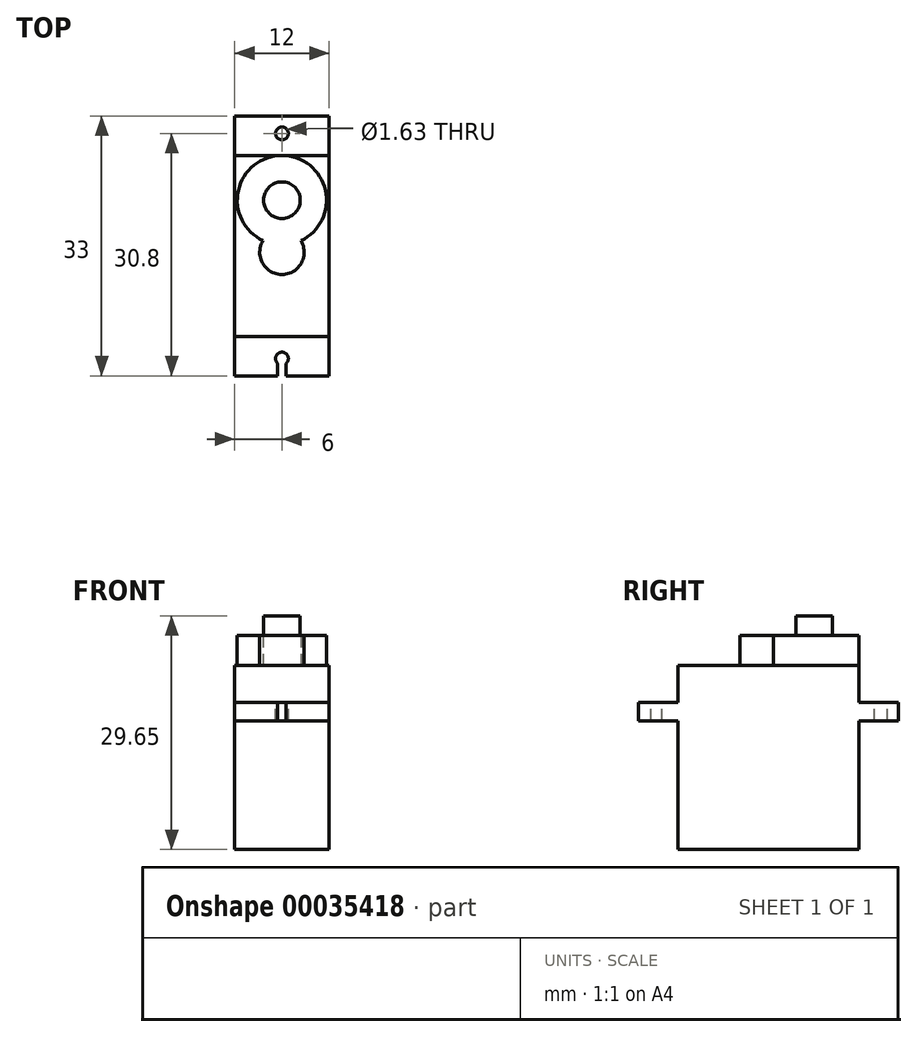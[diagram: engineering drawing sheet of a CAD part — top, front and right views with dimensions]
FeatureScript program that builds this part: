
annotation { "Feature Type Name" : "Feature", "Feature Type Description" : "" }
export const myFeature = defineFeature(function(context is Context, id is Id, definition is map)
    precondition{}
    {
        {
            var Q0;
            Q0=qCreatedBy(makeId("Top.planeOp"),FACE);
            var sketch = newSketch(context, id + "F0", { "sketchPlane" : qUnion([Q0])});
            skLineSegment(sketch, "E0.rect.bottom", {"start": v(-6, -11.5) * mm, "end": v(6, -11.5) * mm});
            skLineSegment(sketch, "E0.rect.top", {"start": v(-6, 11.5) * mm, "end": v(6, 11.5) * mm});
            skLineSegment(sketch, "E0.rect.left", {"start": v(-6, -11.5) * mm, "end": v(-6, 11.5) * mm});
            skLineSegment(sketch, "E0.rect.right", {"start": v(6, -11.5) * mm, "end": v(6, 11.5) * mm});
            skPoint(sketch, "E0.rect.middle", {"position": v(0, 0) * mm});
            skSolve(sketch);
        }
        {
            var Q0;
            Q0 = qSketchRegion(id + "F0", true);
            extrude(context, id + "F1", {"entities" : qUnion([Q0]), "depth" : 23.35 * mm});
        }
        {
            var Q0;
            Q0=makeQuery(id+"F1.opExtrude","SWEPT_FACE",FACE,{"disambiguationData":[OSD([sQuery(id+"F0.wireOp",EDGE,"E0.rect.bottom")])]});
            var sketch = newSketch(context, id + "F2", { "sketchPlane" : qUnion([Q0])});
            skLineSegment(sketch, "E1", {"start": v(-6, 23.35) * mm, "end": v(-6, 16.35) * mm});
            skLineSegment(sketch, "E2", {"start": v(-6, 16.35) * mm, "end": v(-6, 23.35) * mm});
            skLineSegment(sketch, "E3.bottom", {"start": v(-6, 16.35) * mm, "end": v(6, 16.35) * mm});
            skLineSegment(sketch, "E3.top", {"start": v(-6, 18.65) * mm, "end": v(6, 18.65) * mm});
            skLineSegment(sketch, "E3.left", {"start": v(-6, 16.35) * mm, "end": v(-6, 18.65) * mm});
            skLineSegment(sketch, "E3.right", {"start": v(6, 16.35) * mm, "end": v(6, 18.65) * mm});
            skSolve(sketch);
        }
        {
            var Q0;
            Q0 = qSketchRegion(id + "F2", true);
            extrude(context, id + "F3", {"entities" : qUnion([Q0]), "operationType" : NewBodyOperationType.ADD, "depth" : 5 * mm, "hasSecondDirection" : true, "secondDirectionOppositeDirection" : true, "secondDirectionDepth" : 28 * mm});
        }
        {
            var Q0;
            Q0=makeQuery(id+"F1.opExtrude","CAP_FACE",FACE,{"disambiguationData":[OSD([sQuery(id+"F0.wireOp",EDGE,"E0.rect.bottom"),sQuery(id+"F0.wireOp",EDGE,"E0.rect.top"),sQuery(id+"F0.wireOp",EDGE,"E0.rect.left"),sQuery(id+"F0.wireOp",EDGE,"E0.rect.right")])],"isStart":false});
            var sketch = newSketch(context, id + "F4", { "sketchPlane" : qUnion([Q0])});
            skLineSegment(sketch, "E4", {"start": v(0, 11.5) * mm, "end": v(0, 5.82) * mm});
            skPoint(sketch, "E4.endSnap0", {"position": v(0, 11.5) * mm});
            skLineSegment(sketch, "E5", {"start": v(0, 5.82) * mm, "end": v(0, 11.5) * mm});
            skCircle(sketch, "E6", {"center": v(0, 5.82) * mm, "radius": 5.68 * mm});
            skLineSegment(sketch, "E7", {"start": v(0, 11.5) * mm, "end": v(0, -0.8) * mm});
            skLineSegment(sketch, "E8", {"start": v(0, -0.8) * mm, "end": v(0, 11.5) * mm});
            skCircle(sketch, "E9", {"center": v(0, -0.8) * mm, "radius": 2.83 * mm});
            skSolve(sketch);
        }
        {
            var Q0;
            Q0 = qSketchRegion(id + "F4", true);
            extrude(context, id + "F5", {"entities" : qUnion([Q0]), "operationType" : NewBodyOperationType.ADD, "depth" : 3.8 * mm});
        }
        {
            var Q0;
            Q0=makeQuery(id+"F5.opExtrude","CAP_FACE",FACE,{"disambiguationData":[OSD([sQuery(id+"F4.wireOp",EDGE,"E6"),sQuery(id+"F4.wireOp",EDGE,"E9")])],"isStart":false});
            var sketch = newSketch(context, id + "F6", { "sketchPlane" : qUnion([Q0])});
            skCircle(sketch, "E10", {"center": v(0, 5.82) * mm, "radius": 2.33 * mm});
            skSolve(sketch);
        }
        {
            var Q0;
            Q0 = qSketchRegion(id + "F6", true);
            extrude(context, id + "F7", {"entities" : qUnion([Q0]), "operationType" : NewBodyOperationType.ADD, "depth" : 2.5 * mm});
        }
        {
            var Q0;
            {var subQ2=sQuery(id+"F2.wireOp",EDGE,"E3.top");Q0=makeQuery(id+"F3.boolean.opBoolean","SPLIT",FACE,{"disambiguationData":[TD([makeQuery(id+"F1.opExtrude","SWEPT_FACE",FACE,{"disambiguationData":[OSD([sQuery(id+"F0.wireOp",EDGE,"E0.rect.top")])]})])],"derivedFrom":makeQuery(id+"F3.opExtrude","SWEPT_FACE",FACE,{"disambiguationData":[OSD([subQ2])]})});}
            var sketch = newSketch(context, id + "F8", { "sketchPlane" : qUnion([Q0])});
            skLineSegment(sketch, "E11.bottom", {"start": v(-6, 16.5) * mm, "end": v(6, 16.5) * mm});
            skLineSegment(sketch, "E11.top", {"start": v(-6, 16.5) * mm, "end": v(6, 16.5) * mm});
            skLineSegment(sketch, "E11.left", {"start": v(-6, 16.5) * mm, "end": v(-6, 16.5) * mm});
            skLineSegment(sketch, "E11.right", {"start": v(6, 16.5) * mm, "end": v(6, 16.5) * mm});
            skLineSegment(sketch, "E12.bottom", {"start": v(-0.55, 14.9) * mm, "end": v(0.55, 14.9) * mm});
            skLineSegment(sketch, "E12.top", {"start": v(-0.55, 18.1) * mm, "end": v(0.55, 18.1) * mm});
            skLineSegment(sketch, "E12.left", {"start": v(-0.55, 14.9) * mm, "end": v(-0.55, 18.1) * mm});
            skLineSegment(sketch, "E12.right", {"start": v(0.55, 14.9) * mm, "end": v(0.55, 18.1) * mm});
            skPoint(sketch, "E12.middle", {"position": v(0, 16.5) * mm});
            skLineSegment(sketch, "E13", {"start": v(0, 11.5) * mm, "end": v(0, 14.3) * mm});
            skPoint(sketch, "E13.endSnap0", {"position": v(0, 14.9) * mm});
            skLineSegment(sketch, "E14", {"start": v(0, 14.3) * mm, "end": v(0, 11.5) * mm});
            skCircle(sketch, "E15", {"center": v(0, 14.3) * mm, "radius": 0.81 * mm});
            skSolve(sketch);
        }
        {
            var Q0;
            {var subQ0=sQuery(id+"F8.wireOp",EDGE,"E12.bottom");Q0=makeQuery(id+"F8.imprint","IMPRINT",FACE,{"disambiguationData":[TD([[makeQuery(id+"F8.imprint","IMPRINT",EDGE,{"derivedFrom":subQ0}),-1.0]])]});}
            var Q1;
            {var subQ0=sQuery(id+"F8.wireOp",EDGE,"E12.left");var subQ1=sQuery(id+"F8.wireOp",EDGE,"E11.top");var subQ2=makeQuery(id+"F8.imprint","INTERSECT",VERTEX,{"derivedFrom":[subQ1,subQ0]});Q1=makeQuery(id+"F8.imprint","IMPRINT",FACE,{"disambiguationData":[TD([[makeQuery(id+"F8.imprint","IMPRINT",EDGE,{"disambiguationData":[TD([[subQ2,-1.0]])],"derivedFrom":subQ1}),-1.0]])]});}
            var Q2;
            {var subQ0=sQuery(id+"F8.wireOp",EDGE,"E12.bottom");Q2=makeQuery(id+"F8.imprint","IMPRINT",FACE,{"disambiguationData":[TD([[makeQuery(id+"F8.imprint","IMPRINT",EDGE,{"derivedFrom":subQ0}),1.0]])]});}
            extrude(context, id + "F9", {"entities" : qUnion([Q0, Q1, Q2]), "operationType" : NewBodyOperationType.REMOVE, "oppositeDirection" : true, "depth" : 25 * mm});
        }
        {
            var Q0;
            {var subQ2=sQuery(id+"F2.wireOp",EDGE,"E3.top");Q0=makeQuery(id+"F3.boolean.opBoolean","SPLIT",FACE,{"disambiguationData":[TD([makeQuery(id+"F1.opExtrude","SWEPT_FACE",FACE,{"disambiguationData":[OSD([sQuery(id+"F0.wireOp",EDGE,"E0.rect.bottom")])]})])],"derivedFrom":makeQuery(id+"F3.opExtrude","SWEPT_FACE",FACE,{"disambiguationData":[OSD([subQ2])]})});}
            var sketch = newSketch(context, id + "F10", { "sketchPlane" : qUnion([Q0])});
            skLineSegment(sketch, "E16", {"start": v(0, -11.5) * mm, "end": v(0, -14.3) * mm});
            skPoint(sketch, "E16.endSnap0", {"position": v(0, -11.5) * mm});
            skLineSegment(sketch, "E17", {"start": v(0, -14.3) * mm, "end": v(0, -11.5) * mm});
            skLineSegment(sketch, "E18.bottom", {"start": v(-0.55, -14.9) * mm, "end": v(0.55, -14.9) * mm});
            skLineSegment(sketch, "E18.top", {"start": v(-0.55, -18.1) * mm, "end": v(0.55, -18.1) * mm});
            skLineSegment(sketch, "E18.left", {"start": v(-0.55, -14.9) * mm, "end": v(-0.55, -18.1) * mm});
            skLineSegment(sketch, "E18.right", {"start": v(0.55, -14.9) * mm, "end": v(0.55, -18.1) * mm});
            skPoint(sketch, "E18.middle", {"position": v(0, -16.5) * mm});
            skCircle(sketch, "E19", {"center": v(0, -14.3) * mm, "radius": 0.81 * mm});
            skSolve(sketch);
        }
        {
            var Q0;
            Q0 = qSketchRegion(id + "F10", true);
            extrude(context, id + "F11", {"entities" : qUnion([Q0]), "operationType" : NewBodyOperationType.REMOVE, "oppositeDirection" : true, "depth" : 25 * mm});
        }
    });
